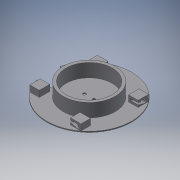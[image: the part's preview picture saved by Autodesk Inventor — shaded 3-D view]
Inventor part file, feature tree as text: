
AUTODESK INVENTOR PART (.ipt)
format: ipt  version: 2016 SP2 (Build 200236200, 236)  size: 258,560 bytes
history: native  units: mm
features: extrude x7, sketch x7, reference x2, pattern_circular x1, projected_geometry x1
ambient origin geometry x8: Origin, YZ Plane, XZ Plane, XY Plane, X Axis, Y Axis, Z Axis, Center Point
bodies: Volumenkörper1 (feature_tree)
feature tree (18):
  extrude  "Extrusion1"  Depth=8.0mm
  extrude  "Extrusion2"  Depth=10.0mm TaperAngle=0.0deg
  extrude  "Extrusion3"  Depth=1.0mm TaperAngle=0.0deg
  extrude  "Extrusion4"  Depth=1.6mm
  pattern_circular  "Runde Anordnung1"  [2 undecoded]
  extrude  "Extrusion5"  Depth=5.0mm
  extrude  "Extrusion6"  Depth=15.0mm
  extrude  "Extrusion7"  Depth=11.0mm
  sketch  "Skizze1"  dims[d0=89.0mm d1=8.0mm]
  sketch  "Skizze2"  dims[d2=40.0mm d4=360.0deg d6=10.0mm d7=0.0mm]
  sketch  "Skizze3"  dims[d8=89.0mm d9=1.0mm d10=0.0mm]
  projected_geometry  "Projizierte Kontur1"
  sketch  "Skizze4"  dims[d11=2.0mm d12=1.6mm]
  sketch  "Skizze5"  dims[d13=15.0deg]
  sketch  "Skizze6"  dims[d14=1.5mm]
  sketch  "Skizze7"  dims[d15=2.0mm d16=2.0mm d17=5.0mm d18=50.974075mm d19=11.0mm d20=6.5mm d21=8.0mm d22=0.0mm d23=2.0mm d24=0.0mm d25=40.0mm d26=360.0deg d28=2.0mm d29=2.0mm d30=2.0mm d31=2.0mm d32=54.5mm d33=3.0mm d34=14.0mm d35=0.0mm d36=15.124913mm d37=8.624913mm d38=1.0mm d39=0.0mm d40=5.0mm d41=3.0mm d42=5.0mm d43=3.0mm d44=10.0mm d45=0.0mm d46=0.2mm d47=0.2mm d48=15.0mm]
  reference  "Referenz3"
  reference  "Referenz4"
note: 2 required parameter values undecoded (feature->parameter linkage not recoverable at this tier; creation-order binding heuristic only, values carry confidence <= 0.55)
